# Revit family: Faucet-Valves_and_Controls-KOHLER-Aqua_Turbo-K-882IN
name_source: partatom
category: Plumbing Fixtures
revit_build: Autodesk Revit 2017 (Build: 20160225_1515(x64)
units: mm (PartAtom-declared; Revit-internal decimal feet)

## family parameters
Cut with Voids When Loaded = No
Host = Face
OmniClass Number = 23.27.31.00
OmniClass Title = Valves
Part Type = Normal
Room Calculation Point = No
Round Connector Dimension = Use Diameter
Shared = No

## types (5) — shared parameters
ADA Compliant = No
CW Connection = Yes
Cold Water Inlet = Cold Water Inlet
Date Modified = 05/29/2020
Default Elevation = 36"
Description = Single-control recessed bath and shower valve (with faceplate diverter)
Drain Included = No
Flow Rate = 0 GPM
HW Connection = Yes
Height = 3 1/8"
Hot Water Inlet = Hot Water Inlet
Length = 5 5/16"
Manufacturer = KOHLER Co.
Master Format 2014 = 22.11.00
Master Format 2014 Name = Residential Faucets, Supplies, and Trim
Material = Solid Brass Construction
Pressure = 0.00 psi
Product Documentation Link = http://resources.kohler.com
Product Name = Aqua Turbo
Product Page URL = https://www.kohler.co.in
Tempered Water Outlet1 = Tempered Water Outlet1
Tempered Water Outlet2 = Tempered Water Outlet2
URL = https://www.kohler.co.in
Vent Connection = No
Waste Connection = No
Waste Water Outlet = Waste Water Outlet
WaterSense Certified = No
Width = 6 5/16"

## per-type parameters (varying)
| type | Assembly Code | Finish | Model | Type |
| RGD-Rose Gold | D2010 | Kohler-Metal-RGD-Polished_Rose_Gold | K-882IN-RGD | 1 |
| AF-French Gold | D2010 | Kohler-Metal-AF-Vibrant_French_Gold | K-882IN-AF | 2 |
| BV-Brushed Bronze | D2010 | Kohler-Metal-BV-Brushed_Bronze | K-882IN-BV | 3 |
| BN-Brushed Nickel | D2010 | Kohler-Metal-BN-Vibrant_Brushed_Nickel | K-882IN-BN | 4 |
| CP-Polished Chrome | D2020 | Kohler-Metal-CP-Polished_Chrome | K-882IN-CP | 5 |

## geometry (parser evidence)
native form markers: Sweep x5
no freeform markers — native parametric forms only
